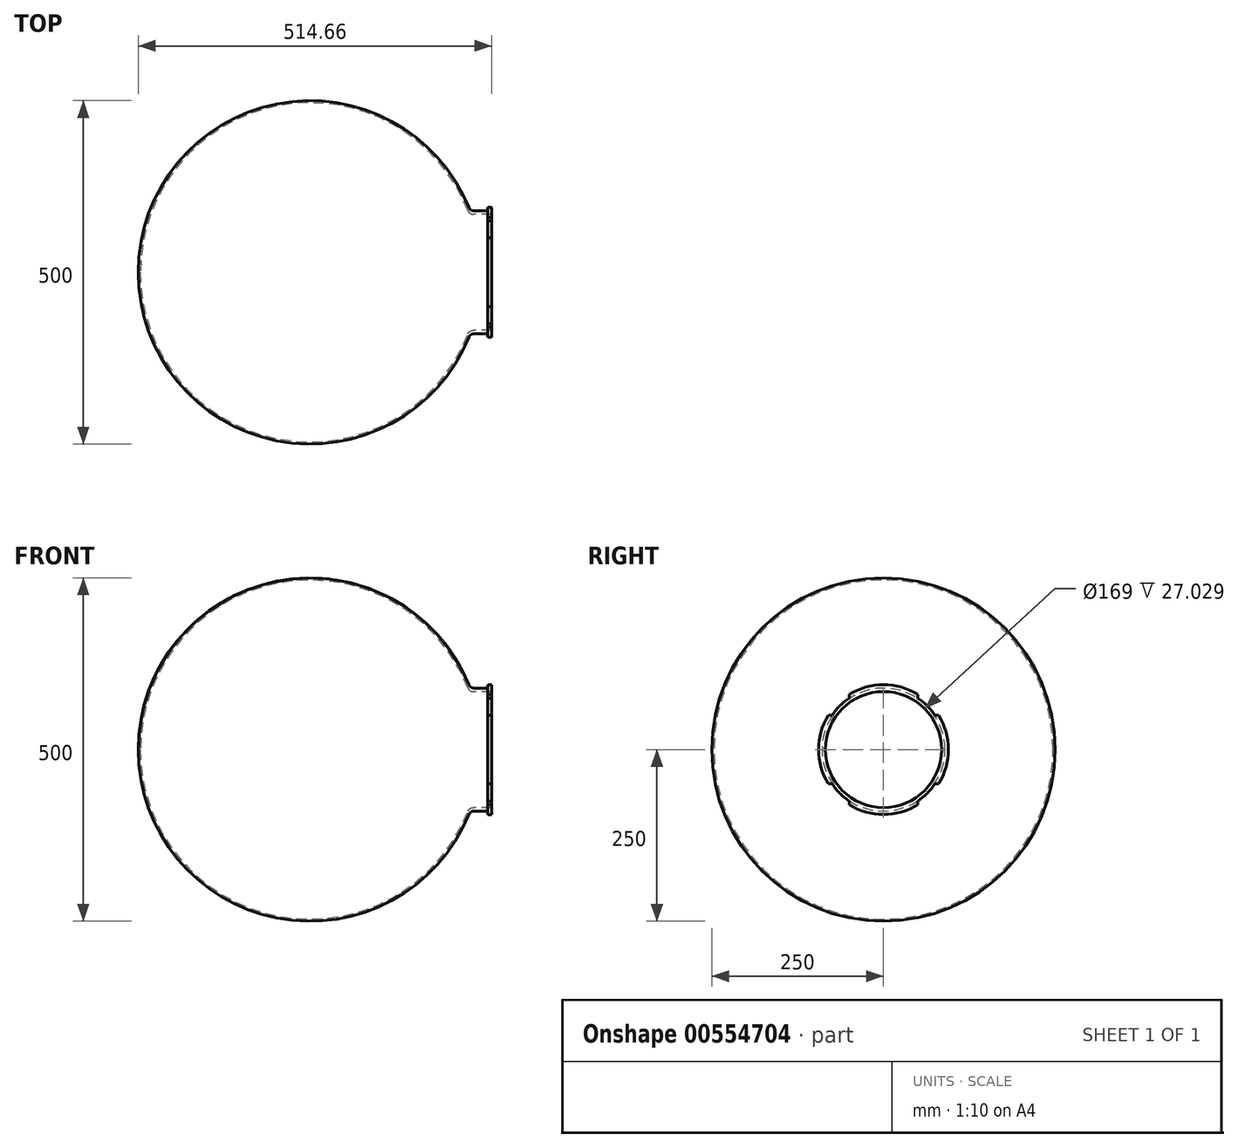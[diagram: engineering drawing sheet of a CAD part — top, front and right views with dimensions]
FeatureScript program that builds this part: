
annotation { "Feature Type Name" : "Feature", "Feature Type Description" : "" }
export const myFeature = defineFeature(function(context is Context, id is Id, definition is map)
    precondition{}
    {
        {
            var Q0;
            Q0=qCreatedBy(makeId("Front.planeOp"),FACE);
            var sketch = newSketch(context, id + "F0", { "sketchPlane" : qUnion([Q0])});
            skArc(sketch, "E0", {"start": v(-247, 0) * mm, "mid": v(-45.58, -242.76) * mm, "end": v(230.18, -89.6) * mm});
            skArc(sketch, "E1", {"start": v(-233.7, 88.77) * mm, "mid": v(-91.63, -232.6) * mm, "end": v(231.46, -94.48) * mm});
            skLineSegment(sketch, "E2.top", {"start": v(264.66, -94.5) * mm, "end": v(258.66, -94.5) * mm});
            skLineSegment(sketch, "E2.left", {"start": v(264.66, -84.5) * mm, "end": v(264.66, -94.5) * mm});
            skLineSegment(sketch, "E3", {"start": v(0, 0) * mm, "end": v(264.66, 0) * mm});
            skLineSegment(sketch, "E4", {"start": v(0, 0) * mm, "end": v(-250, 0) * mm});
            skPoint(sketch, "E2.right.end.orphan", {"position": v(-264.66, -94.5) * mm});
            skPoint(sketch, "E5.orphan", {"position": v(-264.66, 94.5) * mm});
            skLineSegment(sketch, "E6.trimOffspring", {"start": v(-230.5, 88.77) * mm, "end": v(-233.7, 88.77) * mm});
            skPoint(sketch, "E7.orphan", {"position": v(264.66, 94.5) * mm});
            skLineSegment(sketch, "E8", {"start": v(258.66, -94.5) * mm, "end": v(258.66, -89.5) * mm});
            skLineSegment(sketch, "E9", {"start": v(258.66, -89.5) * mm, "end": v(238.87, -89.5) * mm});
            skLineSegment(sketch, "E10", {"start": v(264.66, -84.5) * mm, "end": v(237.63, -84.5) * mm});
            skPoint(sketch, "E11.visualSharp", {"position": v(233.43, -89.5) * mm});
            skArc(sketch, "E11.filletArc", {"start": v(238.87, -89.5) * mm, "mid": v(234.4, -90.86) * mm, "end": v(231.46, -94.48) * mm});
            skPoint(sketch, "E12.visualSharp", {"position": v(232.1, -84.5) * mm});
            skArc(sketch, "E12.filletArc", {"start": v(237.63, -84.5) * mm, "mid": v(233.12, -85.9) * mm, "end": v(230.18, -89.6) * mm});
            skSolve(sketch);
        }
        {
            var Q0;
            {var subQ4=sQuery(id+"F0.wireOp",EDGE,"E0");Q0=makeQuery(id+"F0.imprint","IMPRINT",FACE,{"disambiguationData":[TD([[makeQuery(id+"F0.imprint","IMPRINT",EDGE,{"derivedFrom":subQ4}),-1.0]])]});}
            var Q1;
            Q1=sQuery(id+"F0.wireOp",EDGE,"E3");
            revolve(context, id + "F1", {"entities" : qUnion([Q0]), "axis" : qUnion([Q1]), "revolveType" : RevolveType.FULL});
        }
        {
            var Q0;
            Q0=makeQuery(id+"F1.opRevolve","SWEPT_FACE",FACE,{"disambiguationData":[OSD([sQuery(id+"F0.wireOp",EDGE,"E2.left")])]});
            var sketch = newSketch(context, id + "F2", { "sketchPlane" : qUnion([Q0])});
            skPoint(sketch, "E13.0", {"position": v(0, 0) * mm});
            skCircle(sketch, "E14.0", {"center": v(0, 0) * mm, "radius": 84.5 * mm});
            skCircle(sketch, "E15.0", {"center": v(0, 0) * mm, "radius": 94.5 * mm});
            skCircle(sketch, "E16", {"center": v(0, 0) * mm, "radius": 90 * mm});
            skLineSegment(sketch, "E17.bottom", {"start": v(50, 134.53) * mm, "end": v(-50, 134.53) * mm});
            skLineSegment(sketch, "E17.top", {"start": v(50, -134.53) * mm, "end": v(-50, -134.53) * mm});
            skLineSegment(sketch, "E17.left", {"start": v(50, 134.53) * mm, "end": v(50, -134.53) * mm});
            skLineSegment(sketch, "E17.right", {"start": v(-50, 134.53) * mm, "end": v(-50, -134.53) * mm});
            skLineSegment(sketch, "E18.bottom", {"start": v(-119.59, 50) * mm, "end": v(119.59, 50) * mm});
            skLineSegment(sketch, "E18.top", {"start": v(-119.59, -50) * mm, "end": v(119.59, -50) * mm});
            skLineSegment(sketch, "E18.left", {"start": v(-119.59, 50) * mm, "end": v(-119.59, -50) * mm});
            skLineSegment(sketch, "E18.right", {"start": v(119.59, 50) * mm, "end": v(119.59, -50) * mm});
            skSolve(sketch);
        }
        {
            var Q0;
            {var subQ0=sQuery(id+"F2.wireOp",EDGE,"E17.right");var subQ1=sQuery(id+"F2.wireOp",EDGE,"E15.0");var subQ2=makeQuery(id+"F2.imprint","INTERSECT",VERTEX,{"disambiguationData":[OD(0.0)],"derivedFrom":[subQ1,subQ0]});Q0=makeQuery(id+"F2.imprint","IMPRINT",FACE,{"disambiguationData":[TD([[makeQuery(id+"F2.imprint","IMPRINT",EDGE,{"disambiguationData":[TD([[subQ2,-1.0]])],"derivedFrom":subQ1}),-1.0]])]});}
            var Q1;
            {var subQ0=sQuery(id+"F2.wireOp",EDGE,"E18.bottom");var subQ1=sQuery(id+"F2.wireOp",EDGE,"E15.0");var subQ2=makeQuery(id+"F2.imprint","INTERSECT",VERTEX,{"disambiguationData":[OD(1.0)],"derivedFrom":[subQ1,subQ0]});Q1=makeQuery(id+"F2.imprint","IMPRINT",FACE,{"disambiguationData":[TD([[makeQuery(id+"F2.imprint","IMPRINT",EDGE,{"disambiguationData":[TD([[subQ2,-1.0]])],"derivedFrom":subQ1}),-1.0]])]});}
            var Q2;
            {var subQ0=sQuery(id+"F2.wireOp",EDGE,"E18.bottom");var subQ1=sQuery(id+"F2.wireOp",EDGE,"E15.0");var subQ2=makeQuery(id+"F2.imprint","INTERSECT",VERTEX,{"disambiguationData":[OD(0.0)],"derivedFrom":[subQ1,subQ0]});Q2=makeQuery(id+"F2.imprint","IMPRINT",FACE,{"disambiguationData":[TD([[makeQuery(id+"F2.imprint","IMPRINT",EDGE,{"disambiguationData":[TD([[subQ2,1.0]])],"derivedFrom":subQ1}),-1.0]])]});}
            var Q3;
            {var subQ0=sQuery(id+"F2.wireOp",EDGE,"E18.top");var subQ1=sQuery(id+"F2.wireOp",EDGE,"E15.0");var subQ2=makeQuery(id+"F2.imprint","INTERSECT",VERTEX,{"disambiguationData":[OD(0.0)],"derivedFrom":[subQ1,subQ0]});Q3=makeQuery(id+"F2.imprint","IMPRINT",FACE,{"disambiguationData":[TD([[makeQuery(id+"F2.imprint","IMPRINT",EDGE,{"disambiguationData":[TD([[subQ2,-1.0]])],"derivedFrom":subQ1}),-1.0]])]});}
            extrude(context, id + "F3", {"entities" : qUnion([Q0, Q1, Q2, Q3]), "operationType" : NewBodyOperationType.REMOVE, "oppositeDirection" : true, "depth" : 25 * mm, "offsetDistance" : 25 * mm});
        }
    });
